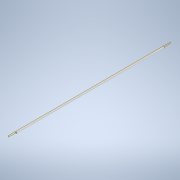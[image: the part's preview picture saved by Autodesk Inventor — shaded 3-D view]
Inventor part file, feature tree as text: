
AUTODESK INVENTOR PART (.ipt)
format: ipt  version: 2021 (Build 250183000, 183)  size: 92,672 bytes
history: native  units: mm
features: extrude x1, plane x1, sketch x1
ambient origin geometry x8: Origin, YZ Plane, XZ Plane, XY Plane, X Axis, Y Axis, Z Axis, Center Point
bodies: Solid1 (feature_tree)
feature tree (3):
  extrude  "Extrusion1"  Depth=6000.0mm TaperAngle=0.0deg
  plane  "Work Plane1"
  sketch  "Sketch1"  dims[d0=53.975mm d1=6000.0mm d2=0.0mm]
